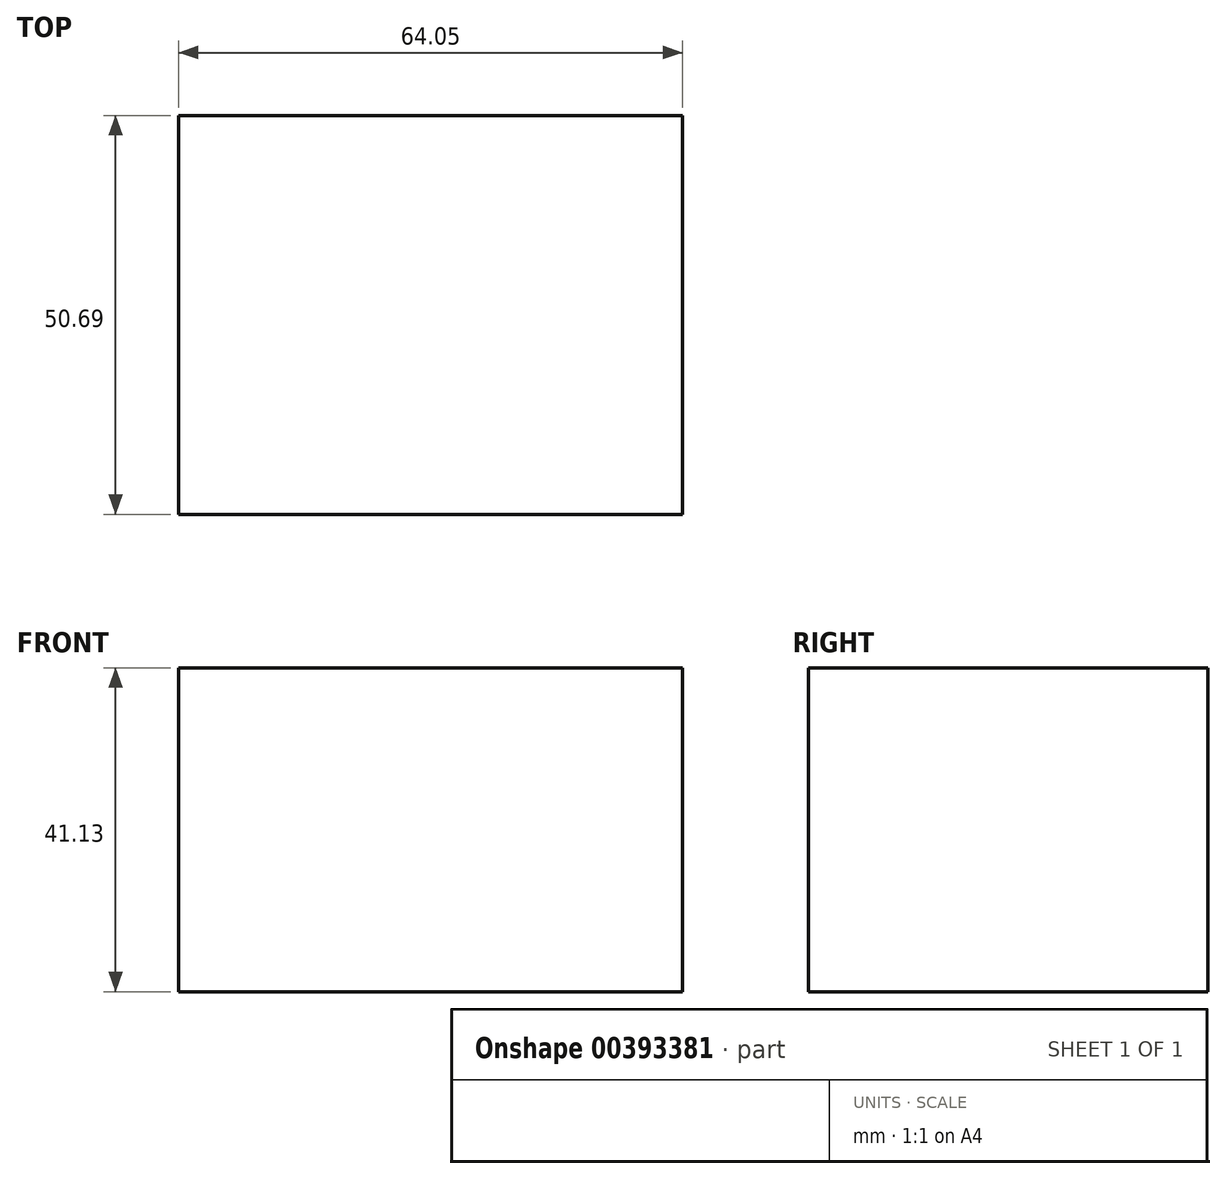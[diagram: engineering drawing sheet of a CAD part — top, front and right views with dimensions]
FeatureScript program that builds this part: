
annotation { "Feature Type Name" : "Feature", "Feature Type Description" : "" }
export const myFeature = defineFeature(function(context is Context, id is Id, definition is map)
    precondition{}
    {
        {
            var Q0;
            Q0=qCreatedBy(makeId("Front.planeOp"),FACE);
            var sketch = newSketch(context, id + "F0", { "sketchPlane" : qUnion([Q0])});
            skLineSegment(sketch, "E0.bottom", {"start": v(64.05, 56.8) * mm, "end": v(0, 56.8) * mm});
            skLineSegment(sketch, "E0.top", {"start": v(64.05, 15.67) * mm, "end": v(0, 15.67) * mm});
            skLineSegment(sketch, "E0.left", {"start": v(64.05, 56.8) * mm, "end": v(64.05, 15.67) * mm});
            skLineSegment(sketch, "E0.right", {"start": v(0, 56.8) * mm, "end": v(0, 15.67) * mm});
            skSolve(sketch);
        }
        {
            var Q0;
            Q0 = qSketchRegion(id + "F0", true);
            extrude(context, id + "F1", {"entities" : qUnion([Q0]), "depth" : 50.69 * mm});
        }
    });
